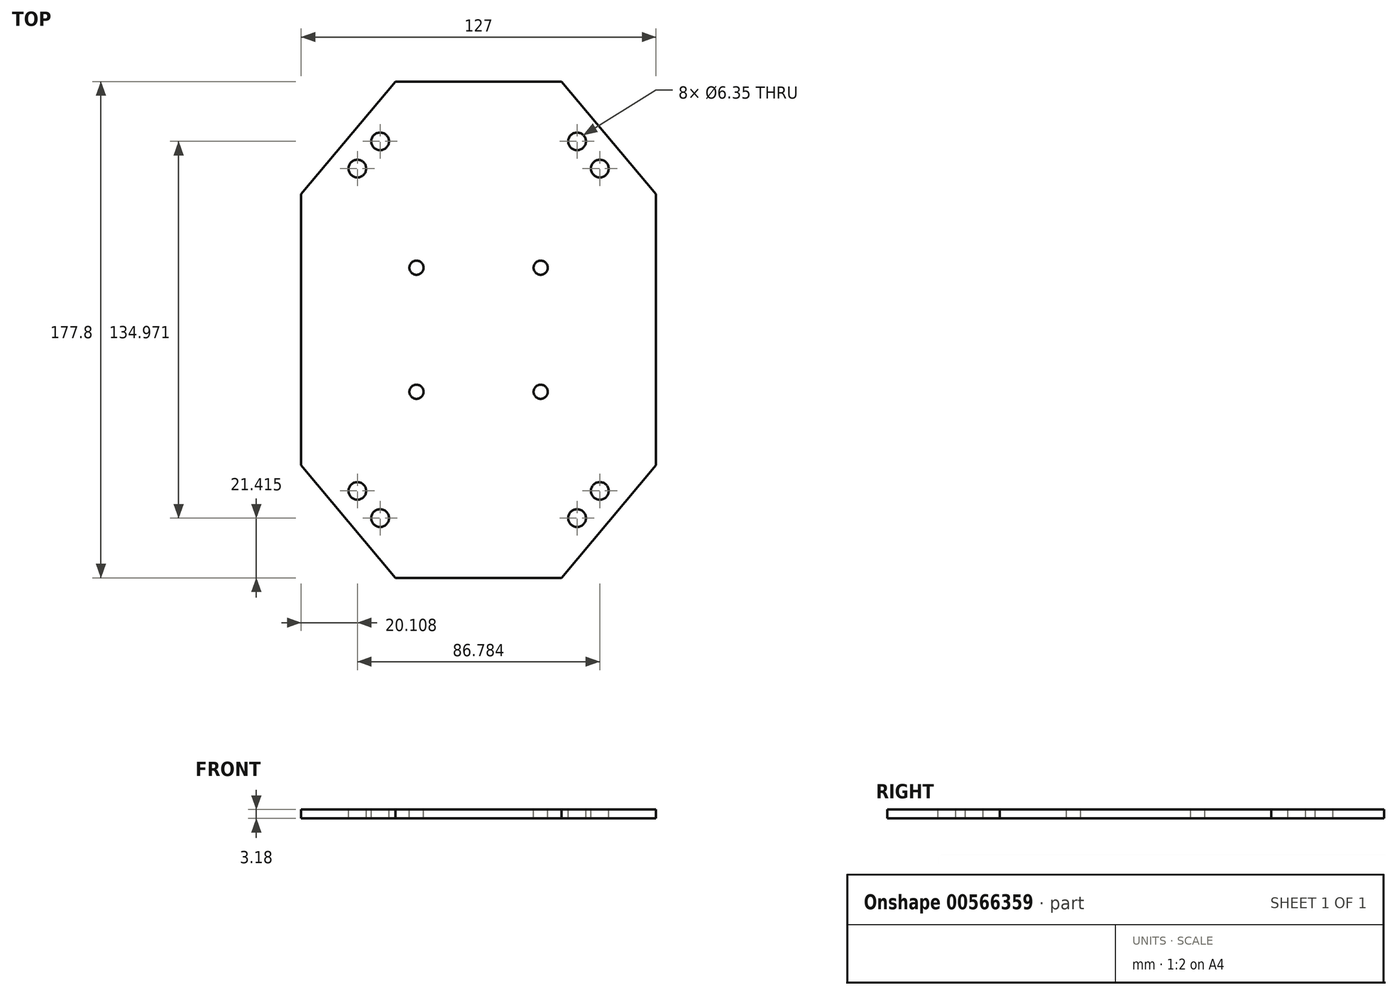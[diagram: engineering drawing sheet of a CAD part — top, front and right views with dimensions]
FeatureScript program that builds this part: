
annotation { "Feature Type Name" : "Feature", "Feature Type Description" : "" }
export const myFeature = defineFeature(function(context is Context, id is Id, definition is map)
    precondition{}
    {
        {
            var Q0;
            Q0=qCreatedBy(makeId("Top.planeOp"),FACE);
            var sketch = newSketch(context, id + "F0", { "sketchPlane" : qUnion([Q0])});
            skLineSegment(sketch, "E0", {"start": v(-29.75, 88.9) * mm, "end": v(29.75, 88.9) * mm});
            skLineSegment(sketch, "E1", {"start": v(29.75, 88.9) * mm, "end": v(63.5, 48.55) * mm});
            skLineSegment(sketch, "E2", {"start": v(63.5, 48.55) * mm, "end": v(63.5, -48.55) * mm});
            skLineSegment(sketch, "E3", {"start": v(63.5, -48.55) * mm, "end": v(29.75, -88.9) * mm});
            skLineSegment(sketch, "E4", {"start": v(29.75, -88.9) * mm, "end": v(-29.75, -88.9) * mm});
            skLineSegment(sketch, "E5", {"start": v(-29.75, -88.9) * mm, "end": v(-63.5, -48.55) * mm});
            skLineSegment(sketch, "E6", {"start": v(-63.5, -48.55) * mm, "end": v(-63.5, 48.55) * mm});
            skLineSegment(sketch, "E7", {"start": v(-63.5, 48.55) * mm, "end": v(-29.75, 88.9) * mm});
            skSolve(sketch);
        }
        {
            var Q0;
            Q0=makeQuery(id+"F0.imprint","IMPRINT",FACE,{"disambiguationData":[TD([[makeQuery(id+"F0.imprint","IMPRINT",EDGE,{"derivedFrom":sQuery(id+"F0.wireOp",EDGE,"E0")}),-1.0]])]});
            extrude(context, id + "F1", {"entities" : qUnion([Q0]), "depth" : 3.17 * mm, "offsetDistance" : 25.4 * mm});
        }
        {
            var Q0;
            Q0=makeQuery(id+"F1.opExtrude","CAP_FACE",FACE,{"disambiguationData":[OSD([sQuery(id+"F0.wireOp",EDGE,"E0"),sQuery(id+"F0.wireOp",EDGE,"E1"),sQuery(id+"F0.wireOp",EDGE,"E2"),sQuery(id+"F0.wireOp",EDGE,"E3"),sQuery(id+"F0.wireOp",EDGE,"E4"),sQuery(id+"F0.wireOp",EDGE,"E5"),sQuery(id+"F0.wireOp",EDGE,"E6"),sQuery(id+"F0.wireOp",EDGE,"E7")])],"isStart":false});
            var sketch = newSketch(context, id + "F2", { "sketchPlane" : qUnion([Q0])});
            skCircle(sketch, "E8", {"center": v(-43.4, 57.74) * mm, "radius": 3.18 * mm});
            skCircle(sketch, "E9", {"center": v(-35.24, 67.49) * mm, "radius": 3.18 * mm});
            skCircle(sketch, "E10", {"center": v(35.24, 67.49) * mm, "radius": 3.18 * mm});
            skCircle(sketch, "E11", {"center": v(43.4, 57.74) * mm, "radius": 3.18 * mm});
            skCircle(sketch, "E12", {"center": v(35.24, -67.49) * mm, "radius": 3.18 * mm});
            skCircle(sketch, "E13", {"center": v(43.4, -57.74) * mm, "radius": 3.18 * mm});
            skCircle(sketch, "E14", {"center": v(-35.24, -67.49) * mm, "radius": 3.18 * mm});
            skCircle(sketch, "E15", {"center": v(-43.4, -57.74) * mm, "radius": 3.18 * mm});
            skSolve(sketch);
        }
        {
            var Q0;
            Q0=makeQuery(id+"F2.imprint","IMPRINT",FACE,{"disambiguationData":[TD([[makeQuery(id+"F2.imprint","IMPRINT",EDGE,{"derivedFrom":sQuery(id+"F2.wireOp",EDGE,"E8")}),1.0]])]});
            var Q1;
            Q1=makeQuery(id+"F2.imprint","IMPRINT",FACE,{"disambiguationData":[TD([[makeQuery(id+"F2.imprint","IMPRINT",EDGE,{"derivedFrom":sQuery(id+"F2.wireOp",EDGE,"E9")}),1.0]])]});
            var Q2;
            Q2=makeQuery(id+"F2.imprint","IMPRINT",FACE,{"disambiguationData":[TD([[makeQuery(id+"F2.imprint","IMPRINT",EDGE,{"derivedFrom":sQuery(id+"F2.wireOp",EDGE,"E10")}),1.0]])]});
            var Q3;
            Q3=makeQuery(id+"F2.imprint","IMPRINT",FACE,{"disambiguationData":[TD([[makeQuery(id+"F2.imprint","IMPRINT",EDGE,{"derivedFrom":sQuery(id+"F2.wireOp",EDGE,"E11")}),1.0]])]});
            var Q4;
            Q4=makeQuery(id+"F2.imprint","IMPRINT",FACE,{"disambiguationData":[TD([[makeQuery(id+"F2.imprint","IMPRINT",EDGE,{"derivedFrom":sQuery(id+"F2.wireOp",EDGE,"E13")}),1.0]])]});
            var Q5;
            Q5=makeQuery(id+"F2.imprint","IMPRINT",FACE,{"disambiguationData":[TD([[makeQuery(id+"F2.imprint","IMPRINT",EDGE,{"derivedFrom":sQuery(id+"F2.wireOp",EDGE,"E12")}),1.0]])]});
            var Q6;
            Q6=makeQuery(id+"F2.imprint","IMPRINT",FACE,{"disambiguationData":[TD([[makeQuery(id+"F2.imprint","IMPRINT",EDGE,{"derivedFrom":sQuery(id+"F2.wireOp",EDGE,"E14")}),1.0]])]});
            var Q7;
            Q7=makeQuery(id+"F2.imprint","IMPRINT",FACE,{"disambiguationData":[TD([[makeQuery(id+"F2.imprint","IMPRINT",EDGE,{"derivedFrom":sQuery(id+"F2.wireOp",EDGE,"E15")}),1.0]])]});
            extrude(context, id + "F3", {"entities" : qUnion([Q0, Q1, Q2, Q3, Q4, Q5, Q6, Q7]), "operationType" : NewBodyOperationType.REMOVE, "oppositeDirection" : true, "depth" : 25.4 * mm, "offsetDistance" : 25.4 * mm});
        }
        {
            var Q0;
            Q0=makeQuery(id+"F1.opExtrude","CAP_FACE",FACE,{"disambiguationData":[OSD([sQuery(id+"F0.wireOp",EDGE,"E0"),sQuery(id+"F0.wireOp",EDGE,"E1"),sQuery(id+"F0.wireOp",EDGE,"E2"),sQuery(id+"F0.wireOp",EDGE,"E3"),sQuery(id+"F0.wireOp",EDGE,"E4"),sQuery(id+"F0.wireOp",EDGE,"E5"),sQuery(id+"F0.wireOp",EDGE,"E6"),sQuery(id+"F0.wireOp",EDGE,"E7")])],"isStart":false});
            var sketch = newSketch(context, id + "F4", { "sketchPlane" : qUnion([Q0])});
            skCircle(sketch, "E16", {"center": v(-22.23, 22.23) * mm, "radius": 2.54 * mm});
            skCircle(sketch, "E17", {"center": v(22.22, 22.23) * mm, "radius": 2.54 * mm});
            skCircle(sketch, "E18", {"center": v(-22.22, -22.22) * mm, "radius": 2.54 * mm});
            skCircle(sketch, "E19", {"center": v(22.23, -22.23) * mm, "radius": 2.54 * mm});
            skSolve(sketch);
        }
        {
            var Q0;
            Q0 = qSketchRegion(id + "F4", true);
            extrude(context, id + "F5", {"entities" : qUnion([Q0]), "operationType" : NewBodyOperationType.REMOVE, "endBound" : BoundingType.THROUGH_ALL, "oppositeDirection" : true, "depth" : 25.4 * mm, "offsetDistance" : 25.4 * mm});
        }
    });
